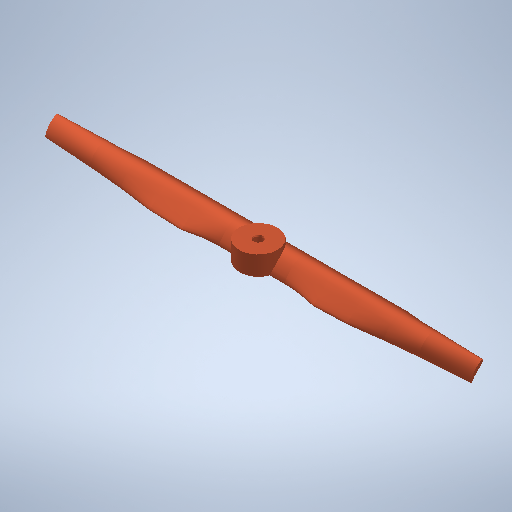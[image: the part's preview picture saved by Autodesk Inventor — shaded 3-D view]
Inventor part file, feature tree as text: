
AUTODESK INVENTOR PART (.ipt)
format: ipt  version: 2025 (Build 290162010, 162A)  size: 626,176 bytes
history: native  units: mm
features: sketch x8, plane x7, loft x5, other x5, mirror x2, revolve x1, hole x1, extrude x1
ambient origin geometry x8: Origin, YZ Plane, XZ Plane, XY Plane, X Axis, Y Axis, Z Axis, Center Point
bodies: Volumenkörper1 (feature_tree)
feature tree (30):
  revolve  "Umdrehung1"
  hole  "Bohrung1"  [1 undecoded]
  plane  "Arbeitsebene2"
  mirror  "Spiegeln1"
  plane  "Arbeitsebene3"
  extrude  "Extrusion2"  [1 undecoded]
  plane  "Arbeitsebene4"
  loft  "Erhebung1"
  plane  "Arbeitsebene5"
  loft  "Erhebung2"
  plane  "Arbeitsebene6"
  loft  "Erhebung3"
  plane  "Arbeitsebene7"
  loft  "Erhebung4"
  plane  "Arbeitsebene8"
  loft  "Erhebung5"
  mirror  "Spiegeln2"
  sketch  "Skizze1"  dims[d0=40.0mm d1=2.0mm]
  sketch  "Skizze2"  dims[d5=90.0deg]
  sketch  "Skizze6"  dims[d6=9.0mm d7=6.0mm d8=10.0mm d9=2.0mm d10=45.0deg d11=10.5mm d12=0.0mm d29=-10.5mm]
  other  "Kanten1"
  other  "Kanten2"
  other  "Kanten3"
  other  "Kanten4"
  other  "Kanten5"
  sketch  "Skizze7"  dims[d30=34.0mm d41=25.8mm]
  sketch  "Skizze8"  dims[d42=10.0mm d43=11.5mm]
  sketch  "Skizze9"  dims[d44=8.0mm d45=3.0mm]
  sketch  "Skizze10"  dims[d46=6.0mm d47=1.0mm]
  sketch  "Skizze11"  dims[d50=10.0mm d52=4.0mm d53=34.0mm d54=0.0mm d55=68.0mm d56=30.8mm d57=10.0mm d58=11.5mm d59=8.0mm d60=3.0mm d62=1.0mm d63=10.0mm d64=4.0mm d65=0.0mm d66=90.0deg d67=0.0mm d68=90.0deg d69=102.0mm d70=29.6mm d71=10.0mm d72=11.5mm d73=8.0mm d74=3.0mm d76=1.0mm d77=10.0mm d78=4.0mm d79=0.0mm d80=90.0deg d81=0.0mm d82=90.0deg d83=136.0mm d84=25.0mm d85=10.0mm d86=11.5mm d87=8.0mm d88=3.0mm d90=1.0mm d91=10.0mm d92=4.0mm d93=0.0mm d94=90.0deg d95=0.0mm d96=90.0deg d97=170.0mm d98=16.3mm d99=7.0mm d100=8.0mm d101=6.0mm d102=3.0mm d104=1.0mm d105=10.0mm d106=4.0mm d107=0.0mm d108=90.0deg d109=0.0mm d110=90.0deg d111=220.0mm d122=0.0mm d123=90.0deg d124=0.0mm d125=90.0deg d127=12.7mm d130=20.0mm d131=21.0mm d132=1.5mm]
note: 2 required parameter values undecoded (feature->parameter linkage not recoverable at this tier; creation-order binding heuristic only, values carry confidence <= 0.55)
